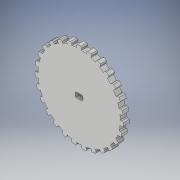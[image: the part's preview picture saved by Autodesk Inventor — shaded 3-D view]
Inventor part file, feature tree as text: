
AUTODESK INVENTOR PART (.ipt)
format: ipt  version: 2017 (Build 210142000, 142)  size: 390,144 bytes
history: native  units: in
note: dims shown in document units (in); Inventor stores cm internally (conversion verified against a paired STEP export)
features: extrude x3, sketch x3, pattern_circular x1
ambient origin geometry x8: Origin, YZ Plane, XZ Plane, XY Plane, X Axis, Y Axis, Z Axis, Center Point
bodies: Solid1 (feature_tree)
feature tree (7):
  extrude  "Extrusion1"  Depth=0.075in
  pattern_circular  "Circular Pattern1"  Count=108 Angle=360.0deg
  extrude  "Extrusion2"  Depth=0.062in
  extrude  "Extrusion3"  Depth=0.062in
  sketch  "Sketch1"  dims[d0=2.025in d4=0.075in]
  sketch  "Sketch2"  dims[d5=0.04in]
  sketch  "Sketch4"  dims[d6=0.04in d7=42.5197in d9=360.0deg d11=0.062in d12=0.062in d13=0.15in d14=0.0in d15=10.6299in d16=360.0deg d18=0.0591in d19=0.15in d20=0.0in d21=0.3862in d22=0.0in]
